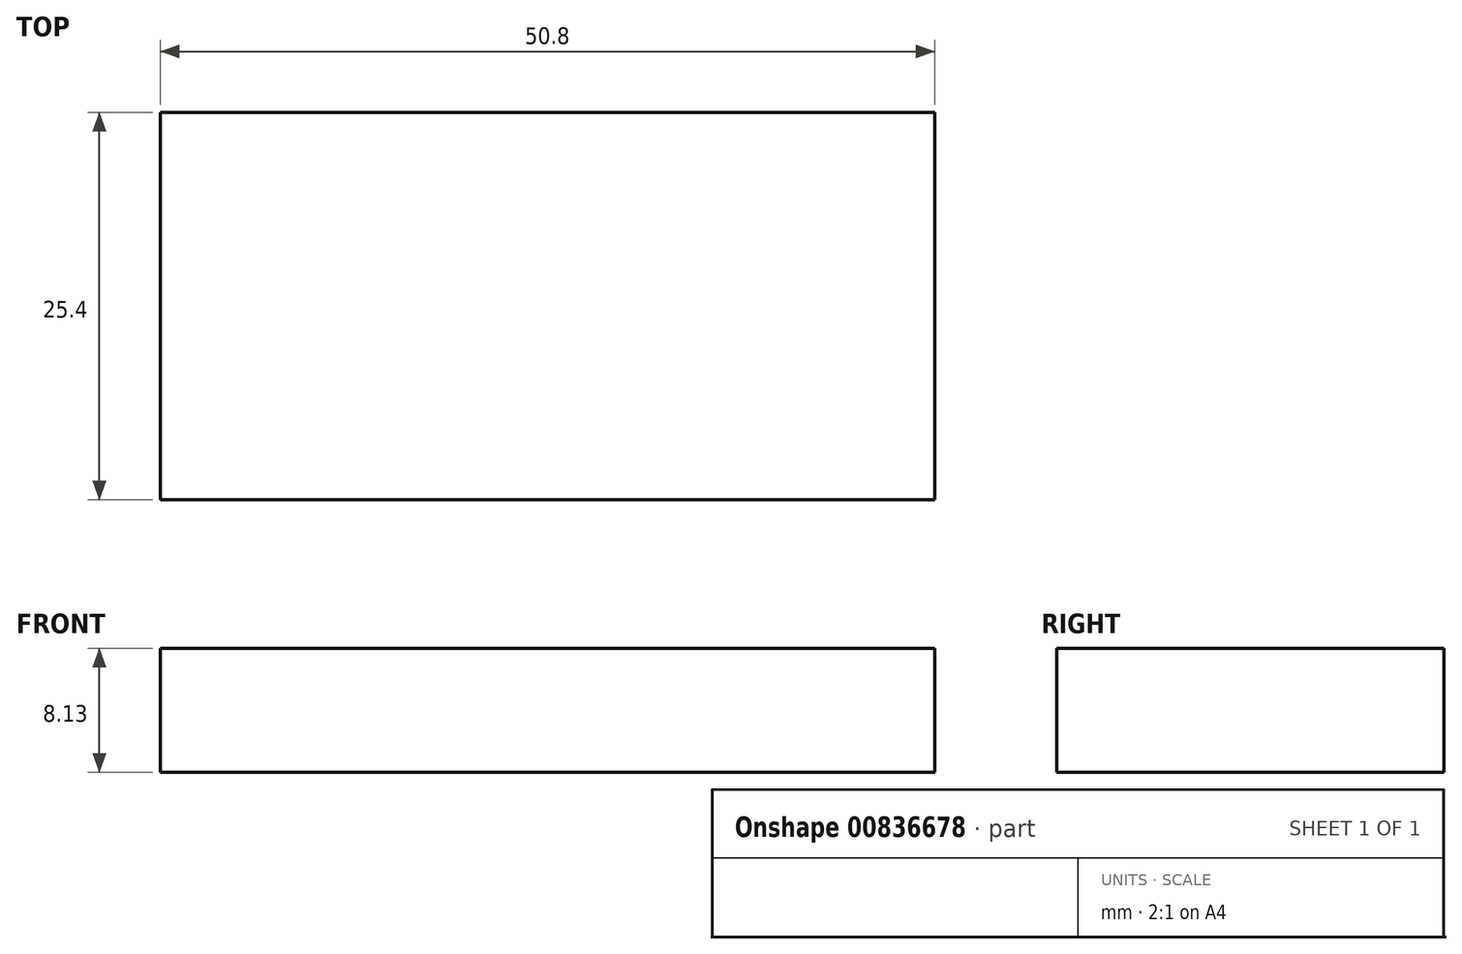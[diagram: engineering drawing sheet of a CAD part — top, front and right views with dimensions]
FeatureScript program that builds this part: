
annotation { "Feature Type Name" : "Feature", "Feature Type Description" : "" }
export const myFeature = defineFeature(function(context is Context, id is Id, definition is map)
    precondition{}
    {
        {
            var Q0;
            Q0=qCreatedBy(makeId("Top.planeOp"),FACE);
            var sketch = newSketch(context, id + "F0", { "sketchPlane" : qUnion([Q0])});
            skLineSegment(sketch, "E0.bottom", {"start": v(0, 0) * mm, "end": v(-50.8, 0) * mm});
            skLineSegment(sketch, "E0.top", {"start": v(0, 25.4) * mm, "end": v(-50.8, 25.4) * mm});
            skLineSegment(sketch, "E0.left", {"start": v(0, 0) * mm, "end": v(0, 25.4) * mm});
            skLineSegment(sketch, "E0.right", {"start": v(-50.8, 0) * mm, "end": v(-50.8, 25.4) * mm});
            skSolve(sketch);
        }
        {
            var Q0;
            Q0=makeQuery(id+"F0.imprint","IMPRINT",FACE,{"disambiguationData":[TD([[makeQuery(id+"F0.imprint","IMPRINT",EDGE,{"derivedFrom":sQuery(id+"F0.wireOp",EDGE,"E0.bottom")}),-1.0]])]});
            extrude(context, id + "F1", {"entities" : qUnion([Q0]), "depth" : 8.13 * mm, "offsetDistance" : 25.4 * mm});
        }
    });
